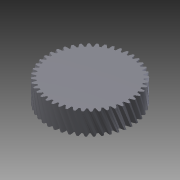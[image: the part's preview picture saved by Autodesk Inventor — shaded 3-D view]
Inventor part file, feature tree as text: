
AUTODESK INVENTOR PART (.ipt)
format: ipt  version: 2012 (Build 160160000, 160)  size: 659,968 bytes
history: native  units: mm (DEFAULTED — no unit token found)
features: plane x3, other x3, sketch x2, extrude x1
ambient origin geometry x8: Origin, YZ Plane, XZ Plane, XY Plane, X Axis, Y Axis, Z Axis, Center Point
bodies: Solid1 (feature_tree)
feature tree (9):
  extrude  "Extrusion1"  Depth=4.0mm TaperAngle=0.0deg
  plane  "Work Plane2"
  plane  "Work Plane8"
  plane  "Work Plane9"
  other  "Spur Gear"
  sketch  "Sketch1"  dims[d0=15.501556mm d1=4.0mm d2=0.0mm]
  sketch  "Sketch2"  dims[d3=14.86278mm d4=10.0mm d5=0.0mm d16=18.071789mm d17=0.0mm d34=0.713998mm d39=0.0mm d41=0.0mm d43=18.071789mm d46=18.071789mm d47=0.0mm d48=0.0mm]
  other  "Srf1"
  other  "Pitch Diameter"
